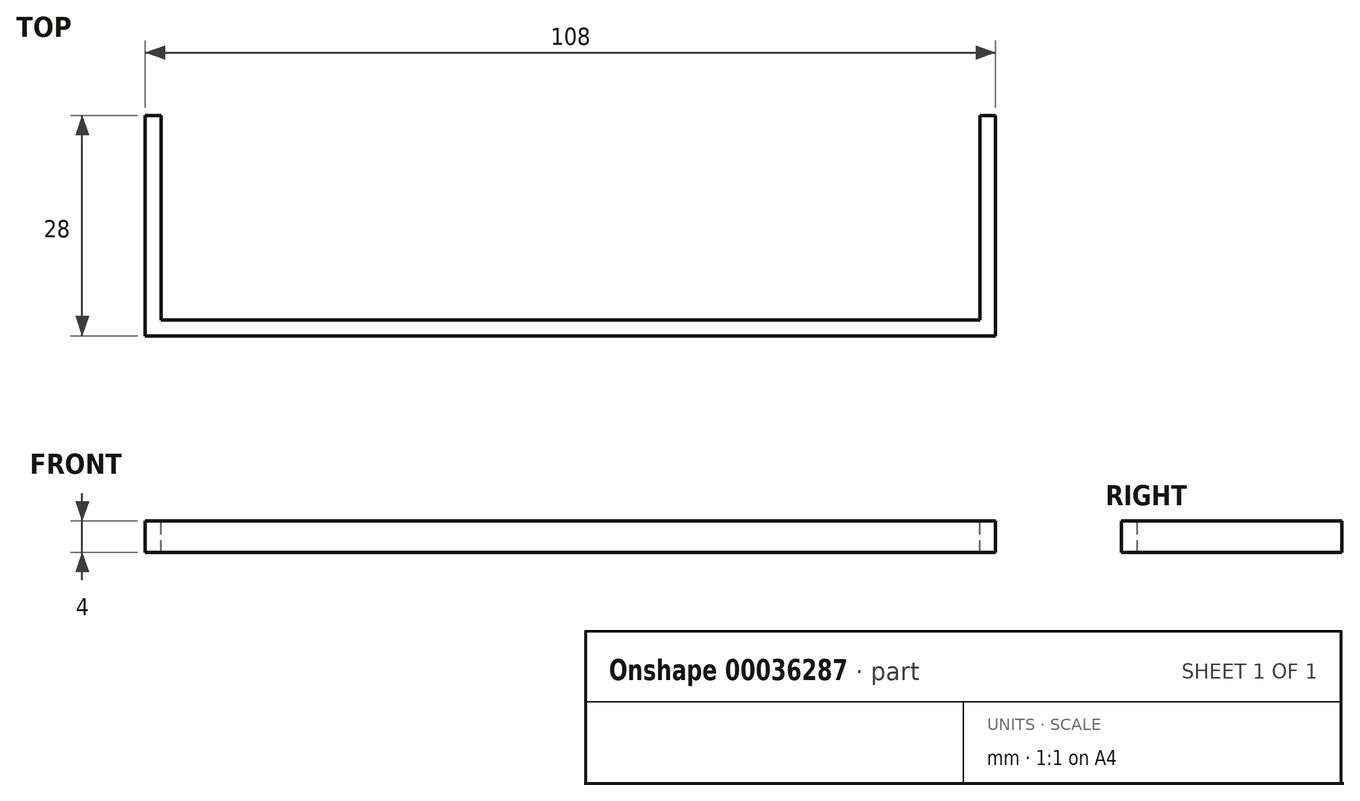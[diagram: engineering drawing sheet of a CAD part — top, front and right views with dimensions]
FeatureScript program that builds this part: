
annotation { "Feature Type Name" : "Feature", "Feature Type Description" : "" }
export const myFeature = defineFeature(function(context is Context, id is Id, definition is map)
    precondition{}
    {
        {
            var Q0;
            Q0=qCreatedBy(makeId("Top.planeOp"),FACE);
            var sketch = newSketch(context, id + "F0", { "sketchPlane" : qUnion([Q0])});
            skLineSegment(sketch, "E0.bottom", {"start": v(108, -30) * mm, "end": v(0, -30) * mm});
            skLineSegment(sketch, "E0.top", {"start": v(108, 0) * mm, "end": v(0, 0) * mm});
            skLineSegment(sketch, "E0.left", {"start": v(108, -30) * mm, "end": v(108, 0) * mm});
            skLineSegment(sketch, "E1", {"start": v(0, -30) * mm, "end": v(0, 0) * mm});
            skPoint(sketch, "E0.right.end.orphan", {"position": v(-106.05, 0) * mm});
            skSolve(sketch);
        }
        {
            var Q0;
            Q0=makeQuery(id+"F0.imprint","IMPRINT",FACE,{"disambiguationData":[TD([[makeQuery(id+"F0.imprint","IMPRINT",EDGE,{"derivedFrom":sQuery(id+"F0.wireOp",EDGE,"E0.bottom")}),-1.0]])]});
            extrude(context, id + "F1", {"entities" : qUnion([Q0]), "oppositeDirection" : true, "depth" : 2 * mm});
        }
        {
            var Q0;
            Q0=makeQuery(id+"F1.opExtrude","CAP_FACE",FACE,{"disambiguationData":[OSD([sQuery(id+"F0.wireOp",EDGE,"E0.bottom"),sQuery(id+"F0.wireOp",EDGE,"E0.top"),sQuery(id+"F0.wireOp",EDGE,"E0.left"),sQuery(id+"F0.wireOp",EDGE,"E1")])],"isStart":false});
            var sketch = newSketch(context, id + "F2", { "sketchPlane" : qUnion([Q0])});
            skLineSegment(sketch, "E2.0", {"start": v(106, 28) * mm, "end": v(2, 28) * mm});
            skLineSegment(sketch, "E2.1", {"start": v(106, 28) * mm, "end": v(106, 2) * mm});
            skLineSegment(sketch, "E2.2", {"start": v(106, 2) * mm, "end": v(2, 2) * mm});
            skLineSegment(sketch, "E2.3", {"start": v(2, 28) * mm, "end": v(2, 2) * mm});
            skLineSegment(sketch, "E3", {"start": v(2, 2) * mm, "end": v(0, 2) * mm});
            skLineSegment(sketch, "E4", {"start": v(106, 2) * mm, "end": v(108, 2) * mm});
            skSolve(sketch);
        }
        {
            var Q0;
            Q0=makeQuery(id+"F2.imprint","IMPRINT",FACE,{"disambiguationData":[TD([[makeQuery(id+"F2.imprint","IMPRINT",EDGE,{"derivedFrom":sQuery(id+"F2.wireOp",EDGE,"E2.0")}),-1.0]])]});
            extrude(context, id + "F3", {"entities" : qUnion([Q0]), "operationType" : NewBodyOperationType.ADD, "depth" : 39 * mm});
        }
        {
            var Q0;
            {var subQ0=sQuery(id+"F0.wireOp",EDGE,"E0.bottom");Q0=makeQuery(id+"F3.boolean.opBoolean","MERGE",FACE,{"derivedFrom":[makeQuery(id+"F1.opExtrude","SWEPT_FACE",FACE,{"disambiguationData":[OSD([subQ0])]}),makeQuery(id+"F3.opExtrude","SWEPT_FACE",FACE,{"disambiguationData":[OSD([subQ0])]})]});}
            var sketch = newSketch(context, id + "F4", { "sketchPlane" : qUnion([Q0])});
            skArc(sketch, "E5", {"start": v(31.19, -24.36) * mm, "mid": v(22.54, -36.75) * mm, "end": v(37.02, -32.4) * mm});
            skLineSegment(sketch, "E6", {"start": v(35.74, -20.94) * mm, "end": v(37.02, -32.4) * mm});
            skLineSegment(sketch, "E7", {"start": v(31.19, -24.36) * mm, "end": v(21.74, -5.32) * mm});
            skFitSpline(sketch, "E8", {"points": [v(35.39, -8.1) * mm, v(48.03, -10.36) * mm, v(54, -20.94) * mm], "startDerivative": vector(20.74, 5.18) * mm, "endDerivative": vector(-9.53, -21.5) * mm});
            skFitSpline(sketch, "E9", {"points": [v(21.74, -5.32) * mm, v(29.02, -9.2) * mm, v(35.39, -8.1) * mm], "startDerivative": vector(11.68, -12.14) * mm, "endDerivative": vector(6.82, 0.29) * mm});
            skFitSpline(sketch, "E10", {"points": [v(35.74, -20.94) * mm, v(43.74, -17.18) * mm, v(54, -20.94) * mm], "startDerivative": vector(27.47, -8.8) * mm, "endDerivative": vector(3.96, -29.24) * mm});
            skSolve(sketch);
        }
        {
            var Q0;
            Q0=qSketchRegion(id+"F4",true);
            extrude(context, id + "F5", {"entities" : qUnion([Q0]), "operationType" : NewBodyOperationType.REMOVE, "endBound" : BoundingType.THROUGH_ALL, "oppositeDirection" : true, "depth" : 25 * mm});
        }
        {
            var Q0;
            Q0=makeQuery(id+"F3.opExtrude","CAP_FACE",FACE,{"disambiguationData":[OSD([sQuery(id+"F0.wireOp",EDGE,"E0.bottom"),sQuery(id+"F0.wireOp",EDGE,"E0.left"),sQuery(id+"F0.wireOp",EDGE,"E1"),sQuery(id+"F2.wireOp",EDGE,"E2.0"),sQuery(id+"F2.wireOp",EDGE,"E2.1"),sQuery(id+"F2.wireOp",EDGE,"E2.3"),sQuery(id+"F2.wireOp",EDGE,"E3"),sQuery(id+"F2.wireOp",EDGE,"E4")])],"isStart":false});
            extrude(context, id + "F6", {"entities" : qUnion([Q0]), "depth" : 4 * mm});
        }
        {
            var Q0;
            Q0=makeQuery(id+"F1.opExtrude","SWEPT_BODY",BODY,{"disambiguationData":[OSD([sQuery(id+"F0.wireOp",EDGE,"E0.bottom"),sQuery(id+"F0.wireOp",EDGE,"E0.top"),sQuery(id+"F0.wireOp",EDGE,"E0.left"),sQuery(id+"F0.wireOp",EDGE,"E1")])]});
            var Q1;
            Q1=makeQuery(id+"F3.opExtrude","CAP_EDGE",EDGE,{"disambiguationData":[OSD([sQuery(id+"F0.wireOp",EDGE,"E0.bottom")])],"isStart":false});
            transform(context, id + "F7", {"entities" : qUnion([Q0]), "transformType" : TransformType.ROTATION, "transformAxis" : qUnion([Q1]), "angle" : 90 * degree, "oppositeDirection" : true, "makeCopy" : false});
        }
        {
            var Q0;
            Q0=makeQuery(id+"F3.opExtrude","CAP_EDGE",EDGE,{"disambiguationData":[OSD([sQuery(id+"F2.wireOp",EDGE,"E2.0")])],"isStart":true});
            var Q1;
            Q1=makeQuery(id+"F3.opExtrude","SWEPT_EDGE",EDGE,{"disambiguationData":[OSD([sQuery(id+"F2.wireOp",EDGE,"E2.0"),sQuery(id+"F2.wireOp",EDGE,"E2.3")])]});
            var Q2;
            Q2=makeQuery(id+"F3.opExtrude","SWEPT_EDGE",EDGE,{"disambiguationData":[OSD([sQuery(id+"F2.wireOp",EDGE,"E2.0"),sQuery(id+"F2.wireOp",EDGE,"E2.1")])]});
            fillet(context, id + "F8", {"entities" : qUnion([Q0, Q1, Q2]), "radius" : 5 * mm, "tangentPropagation" : true, "allowEdgeOverflow" : false});
        }
        {
            var Q0;
            Q0=makeQuery(id+"F1.opExtrude","CAP_FACE",FACE,{"disambiguationData":[OSD([sQuery(id+"F0.wireOp",EDGE,"E0.bottom"),sQuery(id+"F0.wireOp",EDGE,"E0.top"),sQuery(id+"F0.wireOp",EDGE,"E0.left"),sQuery(id+"F0.wireOp",EDGE,"E1")])],"isStart":false});
            var sketch = newSketch(context, id + "F9", { "sketchPlane" : qUnion([Q0])});
            skCircle(sketch, "E11", {"center": v(-22.5, -27.4) * mm, "radius": 2.55 * mm});
            skLineSegment(sketch, "E12.bottom", {"start": v(-46, -29.9) * mm, "end": v(-50, -29.9) * mm});
            skLineSegment(sketch, "E12.top", {"start": v(-46, -25.8) * mm, "end": v(-50, -25.8) * mm});
            skLineSegment(sketch, "E12.left", {"start": v(-44, -27.9) * mm, "end": v(-44, -27.8) * mm});
            skLineSegment(sketch, "E12.right", {"start": v(-52, -27.9) * mm, "end": v(-52, -27.8) * mm});
            skPoint(sketch, "E13.visualSharp", {"position": v(-44, -25.8) * mm});
            skArc(sketch, "E13.filletArc", {"start": v(-44, -27.8) * mm, "mid": v(-44.59, -26.39) * mm, "end": v(-46, -25.8) * mm});
            skPoint(sketch, "E14.visualSharp", {"position": v(-44, -29.9) * mm});
            skArc(sketch, "E14.filletArc", {"start": v(-46, -29.9) * mm, "mid": v(-44.59, -29.31) * mm, "end": v(-44, -27.9) * mm});
            skPoint(sketch, "E15.visualSharp", {"position": v(-52, -29.9) * mm});
            skArc(sketch, "E15.filletArc", {"start": v(-52, -27.9) * mm, "mid": v(-51.41, -29.31) * mm, "end": v(-50, -29.9) * mm});
            skPoint(sketch, "E16.visualSharp", {"position": v(-52, -25.8) * mm});
            skArc(sketch, "E16.filletArc", {"start": v(-50, -25.8) * mm, "mid": v(-51.41, -26.39) * mm, "end": v(-52, -27.8) * mm});
            skLineSegment(sketch, "E17", {"start": v(-48, -29.9) * mm, "end": v(-48, -25.8) * mm, "construction": true});
            skLineSegment(sketch, "E18", {"start": v(-48, -29.9) * mm, "end": v(-48, -32.37) * mm});
            skSolve(sketch);
        }
        {
            var Q0;
            Q0=makeQuery(id+"F9.imprint","IMPRINT",FACE,{"disambiguationData":[TD([[makeQuery(id+"F9.imprint","IMPRINT",EDGE,{"derivedFrom":sQuery(id+"F9.wireOp",EDGE,"E12.bottom")}),-1.0]])]});
            var Q1;
            Q1=makeQuery(id+"F9.imprint","IMPRINT",FACE,{"disambiguationData":[TD([[makeQuery(id+"F9.imprint","IMPRINT",EDGE,{"derivedFrom":sQuery(id+"F9.wireOp",EDGE,"E11")}),1.0]])]});
            extrude(context, id + "F10", {"entities" : qUnion([Q0, Q1]), "operationType" : NewBodyOperationType.REMOVE, "endBound" : BoundingType.THROUGH_ALL, "oppositeDirection" : true, "depth" : 25 * mm});
        }
        {
            var Q0;
            Q0=makeQuery(id+"F1.opExtrude","CAP_FACE",FACE,{"disambiguationData":[OSD([sQuery(id+"F0.wireOp",EDGE,"E0.bottom"),sQuery(id+"F0.wireOp",EDGE,"E0.top"),sQuery(id+"F0.wireOp",EDGE,"E0.left"),sQuery(id+"F0.wireOp",EDGE,"E1")])],"isStart":true});
            var sketch = newSketch(context, id + "F11", { "sketchPlane" : qUnion([Q0])});
            skLineSegment(sketch, "E19", {"start": v(22.5, -27.4) * mm, "end": v(22.5, -41) * mm, "construction": true});
            skLineSegment(sketch, "E20", {"start": v(22.5, -41) * mm, "end": v(32.53, -41) * mm, "construction": true});
            skSolve(sketch);
        }
        {
            var Q0;
            {var subQ0=sQuery(id+"F0.wireOp",EDGE,"E0.bottom");Q0=makeQuery(id+"F3.boolean.opBoolean","MERGE",FACE,{"derivedFrom":[makeQuery(id+"F1.opExtrude","SWEPT_FACE",FACE,{"disambiguationData":[OSD([subQ0])]}),makeQuery(id+"F3.opExtrude","SWEPT_FACE",FACE,{"disambiguationData":[OSD([subQ0])]})]});}
            var sketch = newSketch(context, id + "F12", { "sketchPlane" : qUnion([Q0])});
            skLineSegment(sketch, "E21", {"start": v(32.56, 71) * mm, "end": v(32.56, 49.6) * mm, "construction": true});
            skSolve(sketch);
        }
        {
            var Q0;
            {var subQ4=sQuery(id+"F0.wireOp",EDGE,"E0.bottom");Q0=makeQuery(id+"F12.imprint","IMPRINT",FACE,{"disambiguationData":[TD([[makeQuery(id+"F12.imprint","IMPRINT",EDGE,{"derivedFrom":makeQuery(id+"F3.opExtrude","CAP_EDGE",EDGE,{"disambiguationData":[OSD([subQ4])],"isStart":false})}),-1.0]])]});}
            var sketch = newSketch(context, id + "F13", { "sketchPlane" : qUnion([Q0])});
            skText(sketch, "E22", { "text": "Jr-Asante", "fontName": "AllertaStencil-Regular.ttf"});
            skText(sketch, "E23", { "text": "Balcony", "fontName": "AllertaStencil-Regular.ttf"});
            skText(sketch, "E24", { "text": "Music", "fontName": "AllertaStencil-Regular.ttf"});
            skText(sketch, "E25", { "text": "Makers-Link", "fontName": "AllertaStencil-Regular.ttf"});
            const initialGuessF13  = {"E22": [0.06006, 0.061, 1, 0, 0.006], "E23": [0.06366, 0.051, 1, 0, 0.006], "E24": [0.06897, 0.041, 1, 0, 0.006], "E25": [0.0551, 0.031, 1, 0, 0.006]};
            skSetInitialGuess(sketch, initialGuessF13);
            skSolve(sketch);
        }
        {
            var Q0;
            Q0=qSketchRegion(id+"F13",true);
            extrude(context, id + "F14", {"entities" : qUnion([Q0]), "operationType" : NewBodyOperationType.REMOVE, "endBound" : BoundingType.THROUGH_ALL, "oppositeDirection" : true, "depth" : 25 * mm});
        }
        {
            var Q0;
            {var subQ0=sQuery(id+"F0.wireOp",EDGE,"E0.bottom");Q0=makeQuery(id+"F11.imprint","IMPRINT",FACE,{"disambiguationData":[TD([[makeQuery(id+"F11.imprint","IMPRINT",EDGE,{"derivedFrom":makeQuery(id+"F1.opExtrude","CAP_EDGE",EDGE,{"disambiguationData":[OSD([subQ0])],"isStart":true})}),-1.0]])]});}
            var sketch = newSketch(context, id + "F15", { "sketchPlane" : qUnion([Q0])});
            skText(sketch, "E26", { "text": "AUX", "fontName": "OpenSans-Bold.ttf"});
            skText(sketch, "E27", { "text": "OFF/ON", "fontName": "OpenSans-Bold.ttf"});
            const initialGuessF15  = {"E26": [0.0159, -0.037, 1, 0, 0.0045], "E27": [0.03604, -0.037, 1, 0, 0.0045]};
            skSetInitialGuess(sketch, initialGuessF15);
            skSolve(sketch);
        }
        {
            var Q0;
            Q0=qSketchRegion(id+"F15",true);
            extrude(context, id + "F16", {"entities" : qUnion([Q0]), "operationType" : NewBodyOperationType.REMOVE, "oppositeDirection" : true, "depth" : 0.7 * mm});
        }
        {
            var Q0;
            {var subQ0=sQuery(id+"F0.wireOp",EDGE,"E0.left");Q0=makeQuery(id+"F3.boolean.opBoolean","MERGE",FACE,{"derivedFrom":[makeQuery(id+"F1.opExtrude","SWEPT_FACE",FACE,{"disambiguationData":[OSD([subQ0])]}),makeQuery(id+"F3.opExtrude","SWEPT_FACE",FACE,{"disambiguationData":[OSD([subQ0])]})]});}
            var sketch = newSketch(context, id + "F17", { "sketchPlane" : qUnion([Q0])});
            skLineSegment(sketch, "E28", {"start": v(-32.9, -13) * mm, "end": v(-32.9, -15.3) * mm});
            skLineSegment(sketch, "E29", {"start": v(-34.9, -17.3) * mm, "end": v(-35.1, -17.3) * mm});
            skLineSegment(sketch, "E30", {"start": v(-37.1, -15.3) * mm, "end": v(-37.1, -13) * mm});
            skLineSegment(sketch, "E31", {"start": v(-35, -17.3) * mm, "end": v(-35, -19.69) * mm, "construction": true});
            skPoint(sketch, "E32.visualSharp", {"position": v(-37.1, -17.3) * mm});
            skArc(sketch, "E32.filletArc", {"start": v(-37.1, -15.3) * mm, "mid": v(-36.51, -16.71) * mm, "end": v(-35.1, -17.3) * mm});
            skPoint(sketch, "E33.visualSharp", {"position": v(-32.9, -17.3) * mm});
            skArc(sketch, "E33.filletArc", {"start": v(-34.9, -17.3) * mm, "mid": v(-33.49, -16.71) * mm, "end": v(-32.9, -15.3) * mm});
            skSolve(sketch);
        }
        {
            var Q0;
            {var subQ2=sQuery(id+"F17.wireOp",EDGE,"E28");Q0=makeQuery(id+"F17.imprint","IMPRINT",FACE,{"disambiguationData":[TD([[makeQuery(id+"F17.imprint","IMPRINT",EDGE,{"derivedFrom":subQ2}),-1.0]])]});}
            extrude(context, id + "F18", {"entities" : qUnion([Q0]), "operationType" : NewBodyOperationType.REMOVE, "endBound" : BoundingType.UP_TO_NEXT, "oppositeDirection" : true, "depth" : 25 * mm});
        }
        {
            var Q0;
            Q0=makeQuery(id+"F6.opExtrude","SWEPT_BODY",BODY,{"disambiguationData":[OSD([sQuery(id+"F0.wireOp",EDGE,"E0.bottom"),sQuery(id+"F0.wireOp",EDGE,"E0.left"),sQuery(id+"F0.wireOp",EDGE,"E1"),sQuery(id+"F2.wireOp",EDGE,"E2.0"),sQuery(id+"F2.wireOp",EDGE,"E2.1"),sQuery(id+"F2.wireOp",EDGE,"E2.3"),sQuery(id+"F2.wireOp",EDGE,"E3"),sQuery(id+"F2.wireOp",EDGE,"E4")])]});
            transform(context, id + "F19", {"entities" : qUnion([Q0]), "transformType" : TransformType.TRANSLATION_3D, "dx" : 0 * mm, "dy" : 46.18 * mm, "dz" : 0 * mm, "makeCopy" : true});
        }
        {
            var Q0;
            Q0=makeQuery(id+"F1.opExtrude","SWEPT_BODY",BODY,{"disambiguationData":[OSD([sQuery(id+"F0.wireOp",EDGE,"E0.bottom"),sQuery(id+"F0.wireOp",EDGE,"E0.top"),sQuery(id+"F0.wireOp",EDGE,"E0.left"),sQuery(id+"F0.wireOp",EDGE,"E1")])]});
            var Q1;
            Q1=makeQuery(id+"F19.opPattern","COPY",BODY,{"derivedFrom":makeQuery(id+"F6.opExtrude","SWEPT_BODY",BODY,{"disambiguationData":[OSD([sQuery(id+"F0.wireOp",EDGE,"E0.bottom"),sQuery(id+"F0.wireOp",EDGE,"E0.left"),sQuery(id+"F0.wireOp",EDGE,"E1"),sQuery(id+"F2.wireOp",EDGE,"E2.0"),sQuery(id+"F2.wireOp",EDGE,"E2.1"),sQuery(id+"F2.wireOp",EDGE,"E2.3"),sQuery(id+"F2.wireOp",EDGE,"E3"),sQuery(id+"F2.wireOp",EDGE,"E4")])]}),"instanceName":"1"});
            deleteBodies(context, id + "F20", {"entities" : qUnion([Q0, Q1])});
        }
    });
